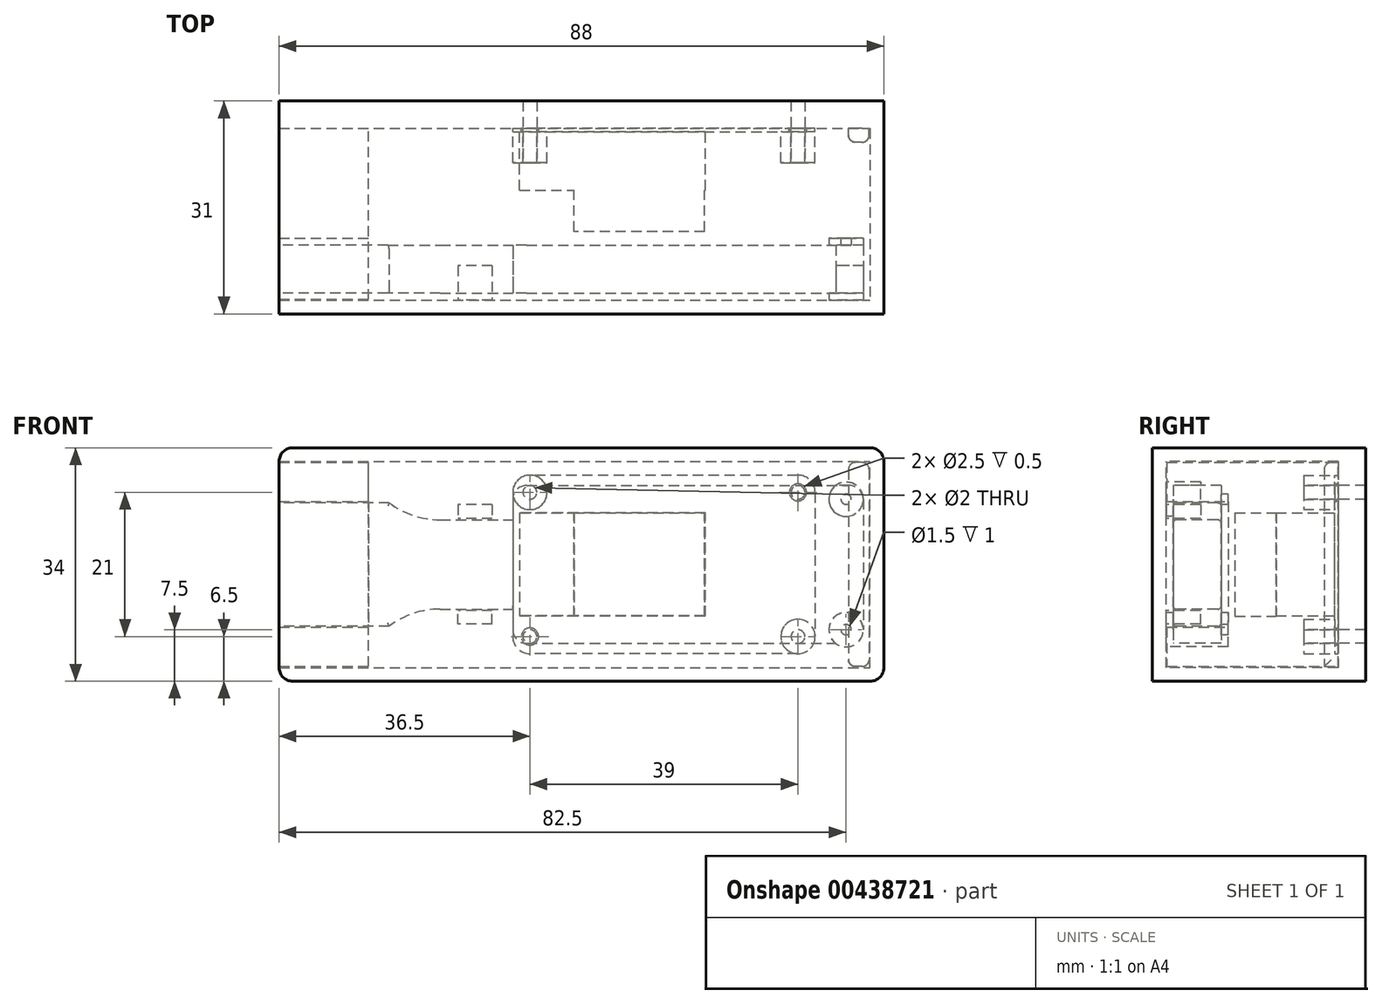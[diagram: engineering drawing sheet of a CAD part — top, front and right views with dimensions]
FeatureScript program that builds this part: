
annotation { "Feature Type Name" : "Feature", "Feature Type Description" : "" }
export const myFeature = defineFeature(function(context is Context, id is Id, definition is map)
    precondition{}
    {
        {
            var Q0;
            Q0=qCreatedBy(makeId("Front.planeOp"),FACE);
            var sketch = newSketch(context, id + "F0", { "sketchPlane" : qUnion([Q0])});
            skLineSegment(sketch, "E0", {"start": v(0, 50.03) * mm, "end": v(0, -37.85) * mm, "construction": true});
            skLineSegment(sketch, "E1", {"start": v(-53.81, 0) * mm, "end": v(52, 0) * mm, "construction": true});
            skLineSegment(sketch, "E2.bottom", {"start": v(-19.5, -13) * mm, "end": v(19.5, -13) * mm});
            skLineSegment(sketch, "E2.top", {"start": v(-19.5, 13) * mm, "end": v(19.5, 13) * mm});
            skLineSegment(sketch, "E2.left", {"start": v(-22, -10.5) * mm, "end": v(-22, 10.5) * mm});
            skLineSegment(sketch, "E2.right", {"start": v(22, -10.5) * mm, "end": v(22, 10.5) * mm});
            skPoint(sketch, "E2.middle", {"position": v(0, 0) * mm});
            skCircle(sketch, "E3", {"center": v(-19.5, -10.5) * mm, "radius": 1.25 * mm});
            skPoint(sketch, "E4.visualSharp", {"position": v(-22, -13) * mm});
            skArc(sketch, "E4.filletArc", {"start": v(-22, -10.5) * mm, "mid": v(-21.27, -12.27) * mm, "end": v(-19.5, -13) * mm});
            skPoint(sketch, "E5.visualSharp", {"position": v(-22, 13) * mm});
            skArc(sketch, "E5.filletArc", {"start": v(-19.5, 13) * mm, "mid": v(-21.27, 12.27) * mm, "end": v(-22, 10.5) * mm});
            skPoint(sketch, "E6.visualSharp", {"position": v(22, 13) * mm});
            skArc(sketch, "E6.filletArc", {"start": v(22, 10.5) * mm, "mid": v(21.27, 12.27) * mm, "end": v(19.5, 13) * mm});
            skPoint(sketch, "E7.visualSharp", {"position": v(22, -13) * mm});
            skArc(sketch, "E7.filletArc", {"start": v(19.5, -13) * mm, "mid": v(21.27, -12.27) * mm, "end": v(22, -10.5) * mm});
            skCircle(sketch, "E8.MirrorC", {"center": v(19.5, -10.5) * mm, "radius": 1.25 * mm});
            skLineSegment(sketch, "E9.MirrorCS", {"start": v(53.81, 0) * mm, "end": v(-52, 0) * mm, "construction": true});
            skCircle(sketch, "E10.MirrorC", {"center": v(-19.5, 10.5) * mm, "radius": 1.25 * mm});
            skCircle(sketch, "E11.MirrorC", {"center": v(19.5, 10.5) * mm, "radius": 1.25 * mm});
            skSolve(sketch);
        }
        {
            var Q0;
            Q0=makeQuery(id+"F0.imprint","IMPRINT",FACE,{"disambiguationData":[TD([[makeQuery(id+"F0.imprint","IMPRINT",EDGE,{"derivedFrom":sQuery(id+"F0.wireOp",EDGE,"E2.bottom")}),1.0]])]});
            extrude(context, id + "F1", {"entities" : qUnion([Q0]), "depth" : 1.5 * mm});
        }
        {
            var Q0;
            Q0=qCreatedBy(makeId("Front.planeOp"),FACE);
            var sketch = newSketch(context, id + "F2", { "sketchPlane" : qUnion([Q0])});
            skLineSegment(sketch, "E12", {"start": v(-65.35, 0) * mm, "end": v(51.32, 0) * mm, "construction": true});
            skLineSegment(sketch, "E13.bottom", {"start": v(-21, 7.5) * mm, "end": v(6, 7.5) * mm});
            skLineSegment(sketch, "E13.top", {"start": v(-21, -7.5) * mm, "end": v(6, -7.5) * mm});
            skLineSegment(sketch, "E13.left", {"start": v(-21, 7.5) * mm, "end": v(-21, -7.5) * mm});
            skLineSegment(sketch, "E13.right", {"start": v(6, 7.5) * mm, "end": v(6, -7.5) * mm});
            skPoint(sketch, "E13.middle", {"position": v(-7.5, 0) * mm});
            skSolve(sketch);
        }
        {
            var Q0;
            Q0=qSketchRegion(id+"F2",true);
            extrude(context, id + "F3", {"entities" : qUnion([Q0]), "operationType" : NewBodyOperationType.ADD, "depth" : 10 * mm});
        }
        {
            var Q0;
            Q0=qCreatedBy(makeId("Front.planeOp"),FACE);
            var sketch = newSketch(context, id + "F4", { "sketchPlane" : qUnion([Q0])});
            skLineSegment(sketch, "E14", {"start": v(-90.91, 0) * mm, "end": v(72.25, 0) * mm, "construction": true});
            skLineSegment(sketch, "E15.bottom", {"start": v(5.93, 7.5) * mm, "end": v(-13.07, 7.5) * mm});
            skLineSegment(sketch, "E15.top", {"start": v(5.93, -7.5) * mm, "end": v(-13.07, -7.5) * mm});
            skLineSegment(sketch, "E15.left", {"start": v(5.93, 7.5) * mm, "end": v(5.93, -7.5) * mm});
            skLineSegment(sketch, "E15.right", {"start": v(-13.07, 7.5) * mm, "end": v(-13.07, -7.5) * mm});
            skSolve(sketch);
        }
        {
            var Q0;
            Q0=qSketchRegion(id+"F4",true);
            extrude(context, id + "F5", {"entities" : qUnion([Q0]), "operationType" : NewBodyOperationType.ADD, "depth" : 16 * mm});
        }
        {
            var Q0;
            Q0=qCreatedBy(makeId("Front.planeOp"),FACE);
            cPlane(context, id + "F6", {"entities" : qUnion([Q0]), "cplaneType" : CPlaneType.OFFSET, "offset" : 25 * mm, "width" : 150 * mm, "height" : 150 * mm});
        }
        {
            var Q0;
            Q0=qCreatedBy(id+"F6.planeOp",FACE);
            var sketch = newSketch(context, id + "F7", { "sketchPlane" : qUnion([Q0])});
            skLineSegment(sketch, "E16.bottom", {"start": v(-22, 11.5) * mm, "end": v(29, 11.5) * mm});
            skLineSegment(sketch, "E16.top", {"start": v(-22, -11.5) * mm, "end": v(29, -11.5) * mm});
            skLineSegment(sketch, "E16.left", {"start": v(-22, 11.5) * mm, "end": v(-22, -11.5) * mm});
            skLineSegment(sketch, "E16.right", {"start": v(29, 11.5) * mm, "end": v(29, -11.5) * mm});
            skPoint(sketch, "E16.middle", {"position": v(3.5, 0) * mm});
            skSolve(sketch);
        }
        {
            var Q0;
            Q0=makeQuery(id+"F7.imprint","IMPRINT",FACE,{"disambiguationData":[TD([[makeQuery(id+"F7.imprint","IMPRINT",EDGE,{"derivedFrom":sQuery(id+"F7.wireOp",EDGE,"E16.bottom")}),-1.0]])]});
            extrude(context, id + "F8", {"entities" : qUnion([Q0]), "oppositeDirection" : true, "depth" : 7 * mm});
        }
        {
            var Q0;
            Q0=makeQuery(id+"F8.opExtrude","SWEPT_EDGE",EDGE,{"disambiguationData":[OSD([sQuery(id+"F7.wireOp",EDGE,"E16.bottom"),sQuery(id+"F7.wireOp",EDGE,"E16.right")])]});
            var Q1;
            Q1=makeQuery(id+"F8.opExtrude","SWEPT_EDGE",EDGE,{"disambiguationData":[OSD([sQuery(id+"F7.wireOp",EDGE,"E16.bottom"),sQuery(id+"F7.wireOp",EDGE,"E16.left")])]});
            var Q2;
            Q2=makeQuery(id+"F8.opExtrude","SWEPT_EDGE",EDGE,{"disambiguationData":[OSD([sQuery(id+"F7.wireOp",EDGE,"E16.top"),sQuery(id+"F7.wireOp",EDGE,"E16.left")])]});
            var Q3;
            Q3=makeQuery(id+"F8.opExtrude","SWEPT_EDGE",EDGE,{"disambiguationData":[OSD([sQuery(id+"F7.wireOp",EDGE,"E16.top"),sQuery(id+"F7.wireOp",EDGE,"E16.right")])]});
            fillet(context, id + "F9", {"entities" : qUnion([Q0, Q1, Q2, Q3]), "radius" : 2 * mm, "tangentPropagation" : true, "allowEdgeOverflow" : false});
        }
        {
            var Q0;
            Q0=qCreatedBy(id+"F6.planeOp",FACE);
            var sketch = newSketch(context, id + "F10", { "sketchPlane" : qUnion([Q0])});
            skLineSegment(sketch, "E17.bottom", {"start": v(-56, 6.5) * mm, "end": v(-22, 6.5) * mm});
            skLineSegment(sketch, "E17.top", {"start": v(-56, -6.5) * mm, "end": v(-22, -6.5) * mm});
            skLineSegment(sketch, "E17.left", {"start": v(-56, 6.5) * mm, "end": v(-56, -6.5) * mm});
            skLineSegment(sketch, "E17.right", {"start": v(-22, 6.5) * mm, "end": v(-22, -6.5) * mm});
            skPoint(sketch, "E17.middle", {"position": v(-39, 0) * mm});
            skLineSegment(sketch, "E18.bottom", {"start": v(-40, -9) * mm, "end": v(-56, -9) * mm});
            skLineSegment(sketch, "E18.top", {"start": v(-40, 9) * mm, "end": v(-56, 9) * mm});
            skLineSegment(sketch, "E18.left", {"start": v(-40, -9) * mm, "end": v(-40, 9) * mm});
            skLineSegment(sketch, "E18.right", {"start": v(-56, -9) * mm, "end": v(-56, 9) * mm});
            skPoint(sketch, "E18.middle", {"position": v(-48, 0) * mm});
            skSolve(sketch);
        }
        {
            var Q0;
            Q0 = qSketchRegion(id + "F10", true);
            extrude(context, id + "F11", {"entities" : qUnion([Q0]), "oppositeDirection" : true, "depth" : 7 * mm});
        }
        {
            var Q0;
            Q0=makeQuery(id+"F11.opExtrude","SWEPT_EDGE",EDGE,{"disambiguationData":[OSD([sQuery(id+"F10.wireOp",EDGE,"E17.bottom"),sQuery(id+"F10.wireOp",EDGE,"E18.left")])]});
            var Q1;
            Q1=makeQuery(id+"F11.opExtrude","SWEPT_EDGE",EDGE,{"disambiguationData":[OSD([sQuery(id+"F10.wireOp",EDGE,"E17.top"),sQuery(id+"F10.wireOp",EDGE,"E18.left")])]});
            fillet(context, id + "F12", {"entities" : qUnion([Q0, Q1]), "radius" : 12.3 * mm, "tangentPropagation" : true, "allowEdgeOverflow" : false});
        }
        {
            var Q0;
            Q0=makeQuery(id+"F11.opExtrude","CAP_EDGE",EDGE,{"disambiguationData":[OSD([sQuery(id+"F10.wireOp",EDGE,"E18.bottom")])],"isStart":false});
            var Q1;
            Q1=makeQuery(id+"F11.opExtrude","CAP_EDGE",EDGE,{"disambiguationData":[OSD([sQuery(id+"F10.wireOp",EDGE,"E17.top")])],"isStart":false});
            var Q2;
            Q2=makeQuery(id+"F11.opExtrude","CAP_EDGE",EDGE,{"disambiguationData":[OSD([sQuery(id+"F10.wireOp",EDGE,"E18.top")])],"isStart":false});
            var Q3;
            {var subQ0=sQuery(id+"F10.wireOp",EDGE,"E18.left");var subQ1=sQuery(id+"F10.wireOp",EDGE,"E17.bottom");Q3=makeQuery(id+"F12.opFillet","BLEND_EDGE",EDGE,{"blendedFrom":[makeQuery(id+"F11.opExtrude","SWEPT_EDGE",EDGE,{"disambiguationData":[OSD([subQ1,subQ0])]}),makeQuery(id+"F11.opExtrude","CAP_FACE",FACE,{"disambiguationData":[OSD([subQ1,sQuery(id+"F10.wireOp",EDGE,"E17.top"),sQuery(id+"F10.wireOp",EDGE,"E17.right"),sQuery(id+"F10.wireOp",EDGE,"E18.bottom"),sQuery(id+"F10.wireOp",EDGE,"E18.top"),subQ0,sQuery(id+"F10.wireOp",EDGE,"E18.right")])],"isStart":false})],"blendedInto":[makeQuery(id+"F11.opExtrude","CAP_FACE",FACE,{"disambiguationData":[OSD([subQ1,sQuery(id+"F10.wireOp",EDGE,"E17.top"),sQuery(id+"F10.wireOp",EDGE,"E17.right"),sQuery(id+"F10.wireOp",EDGE,"E18.bottom"),sQuery(id+"F10.wireOp",EDGE,"E18.top"),subQ0,sQuery(id+"F10.wireOp",EDGE,"E18.right")])],"isStart":false})]});}
            var Q4;
            Q4=makeQuery(id+"F11.opExtrude","CAP_EDGE",EDGE,{"disambiguationData":[OSD([sQuery(id+"F10.wireOp",EDGE,"E17.bottom")])],"isStart":false});
            var Q5;
            {var subQ0=sQuery(id+"F10.wireOp",EDGE,"E18.left");var subQ1=sQuery(id+"F10.wireOp",EDGE,"E17.top");Q5=makeQuery(id+"F12.opFillet","BLEND_EDGE",EDGE,{"blendedFrom":[makeQuery(id+"F11.opExtrude","SWEPT_EDGE",EDGE,{"disambiguationData":[OSD([subQ1,subQ0])]}),makeQuery(id+"F11.opExtrude","CAP_FACE",FACE,{"disambiguationData":[OSD([sQuery(id+"F10.wireOp",EDGE,"E17.bottom"),subQ1,sQuery(id+"F10.wireOp",EDGE,"E17.right"),sQuery(id+"F10.wireOp",EDGE,"E18.bottom"),sQuery(id+"F10.wireOp",EDGE,"E18.top"),subQ0,sQuery(id+"F10.wireOp",EDGE,"E18.right")])],"isStart":false})],"blendedInto":[makeQuery(id+"F11.opExtrude","CAP_FACE",FACE,{"disambiguationData":[OSD([sQuery(id+"F10.wireOp",EDGE,"E17.bottom"),subQ1,sQuery(id+"F10.wireOp",EDGE,"E17.right"),sQuery(id+"F10.wireOp",EDGE,"E18.bottom"),sQuery(id+"F10.wireOp",EDGE,"E18.top"),subQ0,sQuery(id+"F10.wireOp",EDGE,"E18.right")])],"isStart":false})]});}
            var Q6;
            Q6=makeQuery(id+"F11.opExtrude","CAP_EDGE",EDGE,{"disambiguationData":[OSD([sQuery(id+"F10.wireOp",EDGE,"E17.bottom")])],"isStart":true});
            var Q7;
            {var subQ0=sQuery(id+"F10.wireOp",EDGE,"E18.left");var subQ1=sQuery(id+"F10.wireOp",EDGE,"E17.bottom");Q7=makeQuery(id+"F12.opFillet","BLEND_EDGE",EDGE,{"blendedFrom":[makeQuery(id+"F11.opExtrude","SWEPT_EDGE",EDGE,{"disambiguationData":[OSD([subQ1,subQ0])]}),makeQuery(id+"F11.opExtrude","CAP_FACE",FACE,{"disambiguationData":[OSD([subQ1,sQuery(id+"F10.wireOp",EDGE,"E17.top"),sQuery(id+"F10.wireOp",EDGE,"E17.right"),sQuery(id+"F10.wireOp",EDGE,"E18.bottom"),sQuery(id+"F10.wireOp",EDGE,"E18.top"),subQ0,sQuery(id+"F10.wireOp",EDGE,"E18.right")])],"isStart":true})],"blendedInto":[makeQuery(id+"F11.opExtrude","CAP_FACE",FACE,{"disambiguationData":[OSD([subQ1,sQuery(id+"F10.wireOp",EDGE,"E17.top"),sQuery(id+"F10.wireOp",EDGE,"E17.right"),sQuery(id+"F10.wireOp",EDGE,"E18.bottom"),sQuery(id+"F10.wireOp",EDGE,"E18.top"),subQ0,sQuery(id+"F10.wireOp",EDGE,"E18.right")])],"isStart":true})]});}
            var Q8;
            Q8=makeQuery(id+"F11.opExtrude","CAP_EDGE",EDGE,{"disambiguationData":[OSD([sQuery(id+"F10.wireOp",EDGE,"E18.top")])],"isStart":true});
            var Q9;
            Q9=makeQuery(id+"F11.opExtrude","CAP_EDGE",EDGE,{"disambiguationData":[OSD([sQuery(id+"F10.wireOp",EDGE,"E17.top")])],"isStart":true});
            var Q10;
            {var subQ0=sQuery(id+"F10.wireOp",EDGE,"E18.left");var subQ1=sQuery(id+"F10.wireOp",EDGE,"E17.top");Q10=makeQuery(id+"F12.opFillet","BLEND_EDGE",EDGE,{"blendedFrom":[makeQuery(id+"F11.opExtrude","SWEPT_EDGE",EDGE,{"disambiguationData":[OSD([subQ1,subQ0])]}),makeQuery(id+"F11.opExtrude","CAP_FACE",FACE,{"disambiguationData":[OSD([sQuery(id+"F10.wireOp",EDGE,"E17.bottom"),subQ1,sQuery(id+"F10.wireOp",EDGE,"E17.right"),sQuery(id+"F10.wireOp",EDGE,"E18.bottom"),sQuery(id+"F10.wireOp",EDGE,"E18.top"),subQ0,sQuery(id+"F10.wireOp",EDGE,"E18.right")])],"isStart":true})],"blendedInto":[makeQuery(id+"F11.opExtrude","CAP_FACE",FACE,{"disambiguationData":[OSD([sQuery(id+"F10.wireOp",EDGE,"E17.bottom"),subQ1,sQuery(id+"F10.wireOp",EDGE,"E17.right"),sQuery(id+"F10.wireOp",EDGE,"E18.bottom"),sQuery(id+"F10.wireOp",EDGE,"E18.top"),subQ0,sQuery(id+"F10.wireOp",EDGE,"E18.right")])],"isStart":true})]});}
            var Q11;
            Q11=makeQuery(id+"F11.opExtrude","CAP_EDGE",EDGE,{"disambiguationData":[OSD([sQuery(id+"F10.wireOp",EDGE,"E18.bottom")])],"isStart":true});
            fillet(context, id + "F13", {"entities" : qUnion([Q0, Q1, Q2, Q3, Q4, Q5, Q6, Q7, Q8, Q9, Q10, Q11]), "radius" : .5 * mm, "tangentPropagation" : true, "allowEdgeOverflow" : false});
        }
        {
            var Q0;
            Q0=qCreatedBy(id+"F6.planeOp",FACE);
            cPlane(context, id + "F14", {"entities" : qUnion([Q0]), "cplaneType" : CPlaneType.OFFSET, "offset" : 1 * mm, "width" : 150 * mm, "height" : 150 * mm});
        }
        {
            var Q0;
            Q0=qCreatedBy(id+"F14.planeOp",FACE);
            var sketch = newSketch(context, id + "F15", { "sketchPlane" : qUnion([Q0])});
            skLineSegment(sketch, "E19.bottom", {"start": v(-56, -15) * mm, "end": v(30, -15) * mm});
            skLineSegment(sketch, "E19.top", {"start": v(-56, 15) * mm, "end": v(30, 15) * mm});
            skLineSegment(sketch, "E19.left", {"start": v(-56, -15) * mm, "end": v(-56, 15) * mm});
            skLineSegment(sketch, "E19.right", {"start": v(30, -15) * mm, "end": v(30, 15) * mm});
            skPoint(sketch, "E19.middle", {"position": v(-13, 0) * mm});
            skLineSegment(sketch, "E20.0", {"start": v(-56, -17) * mm, "end": v(32, -17) * mm});
            skLineSegment(sketch, "E20.1", {"start": v(32, -17) * mm, "end": v(32, 17) * mm});
            skLineSegment(sketch, "E20.2", {"start": v(-56, 17) * mm, "end": v(32, 17) * mm});
            skLineSegment(sketch, "E21", {"start": v(-56, 17) * mm, "end": v(-56, 15) * mm});
            skLineSegment(sketch, "E22", {"start": v(-56, -17) * mm, "end": v(-56, -15) * mm});
            skSolve(sketch);
        }
        {
            var Q0;
            Q0=makeQuery(id+"F15.imprint","IMPRINT",FACE,{"disambiguationData":[TD([[makeQuery(id+"F15.imprint","IMPRINT",EDGE,{"derivedFrom":sQuery(id+"F15.wireOp",EDGE,"E19.bottom")}),1.0]])]});
            var Q1;
            Q1=makeQuery(id+"F15.imprint","IMPRINT",FACE,{"disambiguationData":[TD([[makeQuery(id+"F15.imprint","IMPRINT",EDGE,{"derivedFrom":sQuery(id+"F15.wireOp",EDGE,"E19.bottom")}),-1.0]])]});
            extrude(context, id + "F16", {"entities" : qUnion([Q0, Q1]), "depth" : 2 * mm});
        }
        {
            var Q0;
            Q0=makeQuery(id+"F15.imprint","IMPRINT",FACE,{"disambiguationData":[TD([[makeQuery(id+"F15.imprint","IMPRINT",EDGE,{"derivedFrom":sQuery(id+"F15.wireOp",EDGE,"E19.bottom")}),-1.0]])]});
            extrude(context, id + "F17", {"entities" : qUnion([Q0]), "operationType" : NewBodyOperationType.ADD, "oppositeDirection" : true, "depth" : 27 * mm});
        }
        {
            var Q0;
            Q0=makeQuery(id+"F17.opExtrude","CAP_FACE",FACE,{"disambiguationData":[OSD([sQuery(id+"F15.wireOp",EDGE,"E19.bottom"),sQuery(id+"F15.wireOp",EDGE,"E19.top"),sQuery(id+"F15.wireOp",EDGE,"E19.right"),sQuery(id+"F15.wireOp",EDGE,"E20.0"),sQuery(id+"F15.wireOp",EDGE,"E20.1"),sQuery(id+"F15.wireOp",EDGE,"E20.2"),sQuery(id+"F15.wireOp",EDGE,"E21"),sQuery(id+"F15.wireOp",EDGE,"E22")])],"isStart":false});
            var sketch = newSketch(context, id + "F18", { "sketchPlane" : qUnion([Q0])});
            skLineSegment(sketch, "E23.bottom", {"start": v(-32, 17) * mm, "end": v(56, 17) * mm});
            skLineSegment(sketch, "E23.top", {"start": v(-32, -17) * mm, "end": v(56, -17) * mm});
            skLineSegment(sketch, "E23.left", {"start": v(-32, 17) * mm, "end": v(-32, -17) * mm});
            skLineSegment(sketch, "E23.right", {"start": v(56, 17) * mm, "end": v(56, -17) * mm});
            skLineSegment(sketch, "E24.bottom", {"start": v(56, 9.15) * mm, "end": v(43, 9.15) * mm});
            skLineSegment(sketch, "E24.top", {"start": v(56, 14.85) * mm, "end": v(43, 14.85) * mm});
            skLineSegment(sketch, "E24.left", {"start": v(56, 9.15) * mm, "end": v(56, 14.85) * mm});
            skLineSegment(sketch, "E24.right", {"start": v(43, 9.15) * mm, "end": v(43, 14.85) * mm});
            skLineSegment(sketch, "E25.bottom", {"start": v(56, -14.85) * mm, "end": v(43, -14.85) * mm});
            skLineSegment(sketch, "E25.top", {"start": v(56, -9.15) * mm, "end": v(43, -9.15) * mm});
            skLineSegment(sketch, "E25.left", {"start": v(56, -14.85) * mm, "end": v(56, -9.15) * mm});
            skLineSegment(sketch, "E25.right", {"start": v(43, -14.85) * mm, "end": v(43, -9.15) * mm});
            skLineSegment(sketch, "E26.left", {"start": v(56, 9.15) * mm, "end": v(56, -9.15) * mm});
            skLineSegment(sketch, "E26.right", {"start": v(43, 9.15) * mm, "end": v(43, -9.15) * mm});
            skCircle(sketch, "E27", {"center": v(-19.5, 10.5) * mm, "radius": 2.5 * mm});
            skCircle(sketch, "E28", {"center": v(-19.5, 10.5) * mm, "radius": 1 * mm});
            skCircle(sketch, "E29.MirrorC", {"center": v(-19.5, -10.5) * mm, "radius": 2.5 * mm});
            skCircle(sketch, "E30.MirrorC", {"center": v(-19.5, -10.5) * mm, "radius": 1 * mm});
            skCircle(sketch, "E31.MirrorC", {"center": v(19.5, 10.5) * mm, "radius": 2.5 * mm});
            skCircle(sketch, "E32.MirrorC", {"center": v(19.5, 10.5) * mm, "radius": 1 * mm});
            skCircle(sketch, "E33.MirrorC", {"center": v(19.5, -10.5) * mm, "radius": 1 * mm});
            skCircle(sketch, "E34.MirrorC", {"center": v(19.5, -10.5) * mm, "radius": 2.5 * mm});
            skLineSegment(sketch, "E35.bottom", {"start": v(-29.85, 14.85) * mm, "end": v(-26.85, 14.85) * mm});
            skLineSegment(sketch, "E35.top", {"start": v(-29.85, -14.85) * mm, "end": v(-26.85, -14.85) * mm});
            skLineSegment(sketch, "E35.left", {"start": v(-29.85, 14.85) * mm, "end": v(-29.85, -14.85) * mm});
            skLineSegment(sketch, "E35.right", {"start": v(-26.85, 14.85) * mm, "end": v(-26.85, -14.85) * mm});
            skLineSegment(sketch, "E36.bottom", {"start": v(28.65, 14.85) * mm, "end": v(43, 14.85) * mm});
            skLineSegment(sketch, "E36.right", {"start": v(43, 14.85) * mm, "end": v(43, 11.85) * mm});
            skLineSegment(sketch, "E37.MirrorCS", {"start": v(28.65, -14.85) * mm, "end": v(43, -14.85) * mm});
            skLineSegment(sketch, "E38.MirrorCS", {"start": v(43, -14.85) * mm, "end": v(43, -11.85) * mm});
            skLineSegment(sketch, "E39.left", {"start": v(56, 5) * mm, "end": v(56, -5) * mm});
            skPoint(sketch, "E40", {"position": v(12, 17) * mm});
            skPoint(sketch, "E41.MirrorCS.start.orphan", {"position": v(17, -27) * mm});
            skSolve(sketch);
        }
        {
            var Q0;
            {var subQ7=sQuery(id+"F18.wireOp",EDGE,"E24.bottom");Q0=makeQuery(id+"F18.imprint","IMPRINT",FACE,{"disambiguationData":[TD([[makeQuery(id+"F18.imprint","IMPRINT",EDGE,{"derivedFrom":subQ7}),1.0]])]});}
            var Q1;
            Q1=makeQuery(id+"F18.imprint","IMPRINT",FACE,{"disambiguationData":[TD([[makeQuery(id+"F18.imprint","IMPRINT",EDGE,{"derivedFrom":sQuery(id+"F18.wireOp",EDGE,"E24.bottom")}),-1.0]])]});
            var Q2;
            Q2=makeQuery(id+"F18.imprint","IMPRINT",FACE,{"disambiguationData":[TD([[makeQuery(id+"F18.imprint","IMPRINT",EDGE,{"derivedFrom":sQuery(id+"F18.wireOp",EDGE,"E25.bottom")}),-1.0]])]});
            var Q3;
            {var subQ3=sQuery(id+"F18.wireOp",EDGE,"E23.bottom");Q3=makeQuery(id+"F18.imprint","IMPRINT",FACE,{"disambiguationData":[TD([[makeQuery(id+"F18.imprint","IMPRINT",EDGE,{"derivedFrom":subQ3}),1.0]])]});}
            var Q4;
            {var subQ0=sQuery(id+"F18.wireOp",EDGE,"E24.top");Q4=makeQuery(id+"F18.imprint","IMPRINT",FACE,{"disambiguationData":[TD([[makeQuery(id+"F18.imprint","IMPRINT",EDGE,{"derivedFrom":subQ0}),-1.0]])]});}
            var Q5;
            Q5=makeQuery(id+"F18.imprint","IMPRINT",FACE,{"disambiguationData":[TD([[makeQuery(id+"F18.imprint","IMPRINT",EDGE,{"derivedFrom":sQuery(id+"F18.wireOp",EDGE,"E24.top")}),1.0]])]});
            var Q6;
            Q6=makeQuery(id+"F18.imprint","IMPRINT",FACE,{"disambiguationData":[TD([[makeQuery(id+"F18.imprint","IMPRINT",EDGE,{"derivedFrom":sQuery(id+"F18.wireOp",EDGE,"E24.bottom")}),1.0]])]});
            var Q7;
            Q7=makeQuery(id+"F18.imprint","IMPRINT",FACE,{"disambiguationData":[TD([[makeQuery(id+"F18.imprint","IMPRINT",EDGE,{"derivedFrom":sQuery(id+"F18.wireOp",EDGE,"E33.MirrorC")}),-1.0]])]});
            var Q8;
            Q8=makeQuery(id+"F18.imprint","IMPRINT",FACE,{"disambiguationData":[TD([[makeQuery(id+"F18.imprint","IMPRINT",EDGE,{"derivedFrom":sQuery(id+"F18.wireOp",EDGE,"E33.MirrorC")}),1.0]])]});
            var Q9;
            Q9=makeQuery(id+"F18.imprint","IMPRINT",FACE,{"disambiguationData":[TD([[makeQuery(id+"F18.imprint","IMPRINT",EDGE,{"derivedFrom":sQuery(id+"F18.wireOp",EDGE,"E31.MirrorC")}),-1.0]])]});
            var Q10;
            Q10=makeQuery(id+"F18.imprint","IMPRINT",FACE,{"disambiguationData":[TD([[makeQuery(id+"F18.imprint","IMPRINT",EDGE,{"derivedFrom":sQuery(id+"F18.wireOp",EDGE,"E32.MirrorC")}),-1.0]])]});
            var Q11;
            Q11=makeQuery(id+"F18.imprint","IMPRINT",FACE,{"disambiguationData":[TD([[makeQuery(id+"F18.imprint","IMPRINT",EDGE,{"derivedFrom":sQuery(id+"F18.wireOp",EDGE,"E27")}),1.0]])]});
            var Q12;
            Q12=makeQuery(id+"F18.imprint","IMPRINT",FACE,{"disambiguationData":[TD([[makeQuery(id+"F18.imprint","IMPRINT",EDGE,{"derivedFrom":sQuery(id+"F18.wireOp",EDGE,"E28")}),1.0]])]});
            var Q13;
            Q13=makeQuery(id+"F18.imprint","IMPRINT",FACE,{"disambiguationData":[TD([[makeQuery(id+"F18.imprint","IMPRINT",EDGE,{"derivedFrom":sQuery(id+"F18.wireOp",EDGE,"E29.MirrorC")}),-1.0]])]});
            var Q14;
            Q14=makeQuery(id+"F18.imprint","IMPRINT",FACE,{"disambiguationData":[TD([[makeQuery(id+"F18.imprint","IMPRINT",EDGE,{"derivedFrom":sQuery(id+"F18.wireOp",EDGE,"E30.MirrorC")}),-1.0]])]});
            var Q15;
            Q15=makeQuery(id+"F18.imprint","IMPRINT",FACE,{"disambiguationData":[TD([[makeQuery(id+"F18.imprint","IMPRINT",EDGE,{"derivedFrom":sQuery(id+"F18.wireOp",EDGE,"E35.bottom")}),-1.0]])]});
            var Q16;
            Q16=makeQuery(id+"F18.imprint","IMPRINT",FACE,{"disambiguationData":[TD([[makeQuery(id+"F18.imprint","IMPRINT",EDGE,{"derivedFrom":sQuery(id+"F18.wireOp",EDGE,"E36.bottom")}),-1.0]])]});
            var Q17;
            Q17=makeQuery(id+"F18.imprint","IMPRINT",FACE,{"disambiguationData":[TD([[makeQuery(id+"F18.imprint","IMPRINT",EDGE,{"derivedFrom":sQuery(id+"F18.wireOp",EDGE,"40c46863-1ba4-41d8-a42c-82d1dc14ebf70.MirrorCS")}),-1.0]])]});
            var Q18;
            {var subQ0=sQuery(id+"F18.wireOp",EDGE,"KswkHpXa-ACxm-TZcQ-8XL7-R7V1whfn34p7");Q18=makeQuery(id+"F18.imprint","IMPRINT",FACE,{"disambiguationData":[TD([[makeQuery(id+"F18.imprint","IMPRINT",EDGE,{"derivedFrom":subQ0}),1.0]])]});}
            var Q19;
            Q19=makeQuery(id+"F18.imprint","IMPRINT",FACE,{"disambiguationData":[TD([[makeQuery(id+"F18.imprint","IMPRINT",EDGE,{"derivedFrom":sQuery(id+"F18.wireOp",EDGE,"fC7vCqkA-tvok-Hrnr-unkS-saNcDAkMh5qa")}),-1.0]])]});
            var Q20;
            {var subQ0=sQuery(id+"F18.wireOp",EDGE,"ac64187c-9d04-435b-9ad2-01fb8e716a770.MirrorCS");Q20=makeQuery(id+"F18.imprint","IMPRINT",FACE,{"disambiguationData":[TD([[makeQuery(id+"F18.imprint","IMPRINT",EDGE,{"derivedFrom":subQ0}),-1.0]])]});}
            var Q21;
            Q21=makeQuery(id+"F18.imprint","IMPRINT",FACE,{"disambiguationData":[TD([[makeQuery(id+"F18.imprint","IMPRINT",EDGE,{"derivedFrom":sQuery(id+"F18.wireOp",EDGE,"cc953e27-e621-4558-ba39-15bed412f6640.MirrorC")}),1.0]])]});
            extrude(context, id + "F19", {"entities" : qUnion([Q0, Q1, Q2, Q3, Q4, Q5, Q6, Q7, Q8, Q9, Q10, Q11, Q12, Q13, Q14, Q15, Q16, Q17, Q18, Q19, Q20, Q21]), "depth" : 2 * mm});
        }
        {
            var Q0;
            Q0=makeQuery(id+"F18.imprint","IMPRINT",FACE,{"disambiguationData":[TD([[makeQuery(id+"F18.imprint","IMPRINT",EDGE,{"derivedFrom":sQuery(id+"F18.wireOp",EDGE,"E24.bottom")}),-1.0]])]});
            var Q1;
            Q1=makeQuery(id+"F18.imprint","IMPRINT",FACE,{"disambiguationData":[TD([[makeQuery(id+"F18.imprint","IMPRINT",EDGE,{"derivedFrom":sQuery(id+"F18.wireOp",EDGE,"E25.bottom")}),-1.0]])]});
            var Q2;
            Q2=makeQuery(id+"F18.imprint","IMPRINT",FACE,{"disambiguationData":[TD([[makeQuery(id+"F18.imprint","IMPRINT",EDGE,{"derivedFrom":sQuery(id+"F18.wireOp",EDGE,"E24.top")}),1.0]])]});
            extrude(context, id + "F20", {"entities" : qUnion([Q0, Q1, Q2]), "operationType" : NewBodyOperationType.ADD, "oppositeDirection" : true, "depth" : 26.9 * mm});
        }
        {
            var Q0;
            Q0=makeQuery(id+"F18.imprint","IMPRINT",FACE,{"disambiguationData":[TD([[makeQuery(id+"F18.imprint","IMPRINT",EDGE,{"derivedFrom":sQuery(id+"F18.wireOp",EDGE,"E24.bottom")}),1.0]])]});
            extrude(context, id + "F21", {"entities" : qUnion([Q0]), "operationType" : NewBodyOperationType.ADD, "oppositeDirection" : true, "depth" : 18 * mm});
        }
        {
            var Q0;
            Q0=makeQuery(id+"F18.imprint","IMPRINT",FACE,{"disambiguationData":[TD([[makeQuery(id+"F18.imprint","IMPRINT",EDGE,{"derivedFrom":sQuery(id+"F18.wireOp",EDGE,"E33.MirrorC")}),-1.0]])]});
            var Q1;
            Q1=makeQuery(id+"F18.imprint","IMPRINT",FACE,{"disambiguationData":[TD([[makeQuery(id+"F18.imprint","IMPRINT",EDGE,{"derivedFrom":sQuery(id+"F18.wireOp",EDGE,"E29.MirrorC")}),-1.0]])]});
            var Q2;
            Q2=makeQuery(id+"F18.imprint","IMPRINT",FACE,{"disambiguationData":[TD([[makeQuery(id+"F18.imprint","IMPRINT",EDGE,{"derivedFrom":sQuery(id+"F18.wireOp",EDGE,"E27")}),1.0]])]});
            var Q3;
            Q3=makeQuery(id+"F18.imprint","IMPRINT",FACE,{"disambiguationData":[TD([[makeQuery(id+"F18.imprint","IMPRINT",EDGE,{"derivedFrom":sQuery(id+"F18.wireOp",EDGE,"E31.MirrorC")}),-1.0]])]});
            extrude(context, id + "F22", {"entities" : qUnion([Q0, Q1, Q2, Q3]), "operationType" : NewBodyOperationType.ADD, "oppositeDirection" : true, "depth" : 2 * mm});
        }
        {
            var Q0;
            Q0=makeQuery(id+"F18.imprint","IMPRINT",FACE,{"disambiguationData":[TD([[makeQuery(id+"F18.imprint","IMPRINT",EDGE,{"derivedFrom":sQuery(id+"F18.wireOp",EDGE,"E28")}),1.0]])]});
            var Q1;
            Q1=makeQuery(id+"F18.imprint","IMPRINT",FACE,{"disambiguationData":[TD([[makeQuery(id+"F18.imprint","IMPRINT",EDGE,{"derivedFrom":sQuery(id+"F18.wireOp",EDGE,"E32.MirrorC")}),-1.0]])]});
            var Q2;
            Q2=makeQuery(id+"F18.imprint","IMPRINT",FACE,{"disambiguationData":[TD([[makeQuery(id+"F18.imprint","IMPRINT",EDGE,{"derivedFrom":sQuery(id+"F18.wireOp",EDGE,"E33.MirrorC")}),1.0]])]});
            var Q3;
            Q3=makeQuery(id+"F18.imprint","IMPRINT",FACE,{"disambiguationData":[TD([[makeQuery(id+"F18.imprint","IMPRINT",EDGE,{"derivedFrom":sQuery(id+"F18.wireOp",EDGE,"E30.MirrorC")}),-1.0]])]});
            extrude(context, id + "F23", {"entities" : qUnion([Q0, Q1, Q2, Q3]), "operationType" : NewBodyOperationType.ADD, "oppositeDirection" : true, "depth" : 7 * mm});
        }
        {
            var Q0;
            Q0=makeQuery(id+"F18.imprint","IMPRINT",FACE,{"disambiguationData":[TD([[makeQuery(id+"F18.imprint","IMPRINT",EDGE,{"derivedFrom":sQuery(id+"F18.wireOp",EDGE,"E35.bottom")}),-1.0]])]});
            extrude(context, id + "F24", {"entities" : qUnion([Q0]), "operationType" : NewBodyOperationType.ADD, "oppositeDirection" : true, "depth" : 4 * mm, "offsetDistance" : 25 * mm});
        }
        {
            var Q0;
            Q0=makeQuery(id+"F24.opExtrude","CAP_EDGE",EDGE,{"disambiguationData":[OSD([sQuery(id+"F18.wireOp",EDGE,"E35.left")])],"isStart":false});
            var Q1;
            Q1=makeQuery(id+"F24.opExtrude","CAP_EDGE",EDGE,{"disambiguationData":[OSD([sQuery(id+"F18.wireOp",EDGE,"E35.bottom")])],"isStart":false});
            var Q2;
            Q2=makeQuery(id+"F24.opExtrude","SWEPT_EDGE",EDGE,{"disambiguationData":[OSD([sQuery(id+"F18.wireOp",EDGE,"E35.bottom"),sQuery(id+"F18.wireOp",EDGE,"E35.left")])]});
            var Q3;
            Q3=makeQuery(id+"F24.opExtrude","SWEPT_EDGE",EDGE,{"disambiguationData":[OSD([sQuery(id+"F18.wireOp",EDGE,"E35.top"),sQuery(id+"F18.wireOp",EDGE,"E35.left")])]});
            var Q4;
            Q4=makeQuery(id+"F24.opExtrude","CAP_EDGE",EDGE,{"disambiguationData":[OSD([sQuery(id+"F18.wireOp",EDGE,"E35.right")])],"isStart":false});
            var Q5;
            Q5=makeQuery(id+"F24.opExtrude","SWEPT_EDGE",EDGE,{"disambiguationData":[OSD([sQuery(id+"F18.wireOp",EDGE,"E35.top"),sQuery(id+"F18.wireOp",EDGE,"E35.right")])]});
            var Q6;
            Q6=makeQuery(id+"F24.opExtrude","SWEPT_EDGE",EDGE,{"disambiguationData":[OSD([sQuery(id+"F18.wireOp",EDGE,"E35.bottom"),sQuery(id+"F18.wireOp",EDGE,"E35.right")])]});
            var Q7;
            Q7=makeQuery(id+"F24.opExtrude","CAP_EDGE",EDGE,{"disambiguationData":[OSD([sQuery(id+"F18.wireOp",EDGE,"E36.bottom")])],"isStart":false});
            var Q8;
            Q8=makeQuery(id+"F24.opExtrude","SWEPT_EDGE",EDGE,{"disambiguationData":[OSD([sQuery(id+"F18.wireOp",EDGE,"E36.bottom"),sQuery(id+"F18.wireOp",EDGE,"E36.left")])]});
            var Q9;
            Q9=makeQuery(id+"F24.opExtrude","CAP_EDGE",EDGE,{"disambiguationData":[OSD([sQuery(id+"F18.wireOp",EDGE,"E36.left")])],"isStart":false});
            var Q10;
            Q10=makeQuery(id+"F24.opExtrude","CAP_EDGE",EDGE,{"disambiguationData":[OSD([sQuery(id+"F18.wireOp",EDGE,"E36.top")])],"isStart":false});
            var Q11;
            Q11=makeQuery(id+"F24.opExtrude","SWEPT_EDGE",EDGE,{"disambiguationData":[OSD([sQuery(id+"F18.wireOp",EDGE,"E36.top"),sQuery(id+"F18.wireOp",EDGE,"E36.left")])]});
            var Q12;
            Q12=makeQuery(id+"F24.opExtrude","CAP_EDGE",EDGE,{"disambiguationData":[OSD([sQuery(id+"F18.wireOp",EDGE,"E37.MirrorCS")])],"isStart":false});
            var Q13;
            Q13=makeQuery(id+"F24.opExtrude","SWEPT_EDGE",EDGE,{"disambiguationData":[OSD([sQuery(id+"F18.wireOp",EDGE,"81e1bee7-cabf-44c3-a33a-e5a7b065c3f50.MirrorCS"),sQuery(id+"F18.wireOp",EDGE,"E37.MirrorCS")])]});
            var Q14;
            Q14=makeQuery(id+"F24.opExtrude","CAP_EDGE",EDGE,{"disambiguationData":[OSD([sQuery(id+"F18.wireOp",EDGE,"81e1bee7-cabf-44c3-a33a-e5a7b065c3f50.MirrorCS")])],"isStart":false});
            var Q15;
            Q15=makeQuery(id+"F24.opExtrude","CAP_EDGE",EDGE,{"disambiguationData":[OSD([sQuery(id+"F18.wireOp",EDGE,"40c46863-1ba4-41d8-a42c-82d1dc14ebf70.MirrorCS")])],"isStart":false});
            var Q16;
            Q16=makeQuery(id+"F24.opExtrude","SWEPT_EDGE",EDGE,{"disambiguationData":[OSD([sQuery(id+"F18.wireOp",EDGE,"40c46863-1ba4-41d8-a42c-82d1dc14ebf70.MirrorCS"),sQuery(id+"F18.wireOp",EDGE,"81e1bee7-cabf-44c3-a33a-e5a7b065c3f50.MirrorCS")])]});
            fillet(context, id + "F25", {"entities" : qUnion([Q0, Q1, Q2, Q3, Q4, Q5, Q6, Q7, Q8, Q9, Q10, Q11, Q12, Q13, Q14, Q15, Q16]), "radius" : 1 * mm, "tangentPropagation" : true, "allowEdgeOverflow" : false});
        }
        {
            var Q0;
            Q0=qCreatedBy(id+"F14.planeOp",FACE);
            var sketch = newSketch(context, id + "F26", { "sketchPlane" : qUnion([Q0])});
            skLineSegment(sketch, "E42.bottom", {"start": v(26.5, 9.5) * mm, "end": v(-19.5, 9.5) * mm, "construction": true});
            skLineSegment(sketch, "E42.top", {"start": v(26.5, -9.5) * mm, "end": v(-19.5, -9.5) * mm, "construction": true});
            skLineSegment(sketch, "E42.left", {"start": v(26.5, 9.5) * mm, "end": v(26.5, -9.5) * mm, "construction": true});
            skLineSegment(sketch, "E42.right", {"start": v(-19.5, 9.5) * mm, "end": v(-19.5, -9.5) * mm, "construction": true});
            skPoint(sketch, "E42.middle", {"position": v(3.5, 0) * mm});
            skCircle(sketch, "E43", {"center": v(26.5, 9.5) * mm, "radius": 2.5 * mm});
            skCircle(sketch, "E44", {"center": v(26.5, 9.5) * mm, "radius": 0.75 * mm});
            skCircle(sketch, "E45.MirrorC", {"center": v(26.5, -9.5) * mm, "radius": 0.75 * mm});
            skCircle(sketch, "E46.MirrorC", {"center": v(26.5, -9.5) * mm, "radius": 2.5 * mm});
            skLineSegment(sketch, "E47.bottom", {"start": v(-25, 8.7) * mm, "end": v(-30, 8.7) * mm});
            skLineSegment(sketch, "E47.top", {"start": v(-25, 6.7) * mm, "end": v(-30, 6.7) * mm});
            skLineSegment(sketch, "E47.left", {"start": v(-25, 8.7) * mm, "end": v(-25, 6.7) * mm});
            skLineSegment(sketch, "E47.right", {"start": v(-30, 8.7) * mm, "end": v(-30, 6.7) * mm});
            skLineSegment(sketch, "E48.MirrorCS", {"start": v(-25, -6.7) * mm, "end": v(-30, -6.7) * mm});
            skLineSegment(sketch, "E49.MirrorCS", {"start": v(-25, -8.7) * mm, "end": v(-25, -6.7) * mm});
            skLineSegment(sketch, "E50.MirrorCS", {"start": v(-25, -8.7) * mm, "end": v(-30, -8.7) * mm});
            skLineSegment(sketch, "E51.MirrorCS", {"start": v(-30, -8.7) * mm, "end": v(-30, -6.7) * mm});
            skSolve(sketch);
        }
        {
            var Q0;
            Q0=makeQuery(id+"F26.imprint","IMPRINT",FACE,{"disambiguationData":[TD([[makeQuery(id+"F26.imprint","IMPRINT",EDGE,{"derivedFrom":sQuery(id+"F26.wireOp",EDGE,"E43")}),1.0]])]});
            var Q1;
            Q1=makeQuery(id+"F26.imprint","IMPRINT",FACE,{"disambiguationData":[TD([[makeQuery(id+"F26.imprint","IMPRINT",EDGE,{"derivedFrom":sQuery(id+"F26.wireOp",EDGE,"E45.MirrorC")}),1.0]])]});
            extrude(context, id + "F27", {"entities" : qUnion([Q0, Q1]), "operationType" : NewBodyOperationType.ADD, "oppositeDirection" : true, "depth" : 5 * mm});
        }
        {
            var Q0;
            Q0=makeQuery(id+"F26.imprint","IMPRINT",FACE,{"disambiguationData":[TD([[makeQuery(id+"F26.imprint","IMPRINT",EDGE,{"derivedFrom":sQuery(id+"F26.wireOp",EDGE,"E44")}),1.0]])]});
            var Q1;
            Q1=makeQuery(id+"F26.imprint","IMPRINT",FACE,{"disambiguationData":[TD([[makeQuery(id+"F26.imprint","IMPRINT",EDGE,{"derivedFrom":sQuery(id+"F26.wireOp",EDGE,"E45.MirrorC")}),-1.0]])]});
            extrude(context, id + "F28", {"entities" : qUnion([Q0, Q1]), "operationType" : NewBodyOperationType.ADD, "oppositeDirection" : true, "depth" : 9 * mm});
        }
        {
            var Q0;
            Q0=makeQuery(id+"F26.imprint","IMPRINT",FACE,{"disambiguationData":[TD([[makeQuery(id+"F26.imprint","IMPRINT",EDGE,{"derivedFrom":sQuery(id+"F26.wireOp",EDGE,"E47.bottom")}),1.0]])]});
            var Q1;
            Q1=makeQuery(id+"F26.imprint","IMPRINT",FACE,{"disambiguationData":[TD([[makeQuery(id+"F26.imprint","IMPRINT",EDGE,{"derivedFrom":sQuery(id+"F26.wireOp",EDGE,"E48.MirrorCS")}),1.0]])]});
            extrude(context, id + "F29", {"entities" : qUnion([Q0, Q1]), "operationType" : NewBodyOperationType.ADD, "oppositeDirection" : true, "depth" : 5 * mm});
        }
        {
            var Q0;
            Q0=makeQuery(id+"F19.opExtrude","SWEPT_EDGE",EDGE,{"disambiguationData":[OSD([sQuery(id+"F18.wireOp",EDGE,"E23.bottom"),sQuery(id+"F18.wireOp",EDGE,"KswkHpXa-ACxm-TZcQ-8XL7-R7V1whfn34p7")])]});
            var Q1;
            Q1=makeQuery(id+"F19.opExtrude","SWEPT_EDGE",EDGE,{"disambiguationData":[OSD([sQuery(id+"F18.wireOp",EDGE,"E23.bottom"),sQuery(id+"F18.wireOp",EDGE,"OMIQOoRZ-lq9q-m5jm-AfYc-Us6GeULHy3RY")])]});
            var Q2;
            Q2=makeQuery(id+"F19.opExtrude","SWEPT_EDGE",EDGE,{"disambiguationData":[OSD([sQuery(id+"F18.wireOp",EDGE,"E23.top"),sQuery(id+"F18.wireOp",EDGE,"E41.MirrorCS")])]});
            var Q3;
            Q3=makeQuery(id+"F19.opExtrude","SWEPT_EDGE",EDGE,{"disambiguationData":[OSD([sQuery(id+"F18.wireOp",EDGE,"E23.top"),sQuery(id+"F18.wireOp",EDGE,"ac64187c-9d04-435b-9ad2-01fb8e716a770.MirrorCS")])]});
            fillet(context, id + "F30", {"entities" : qUnion([Q0, Q1, Q2, Q3]), "radius" : 2 * mm, "tangentPropagation" : true, "allowEdgeOverflow" : false});
        }
    });
